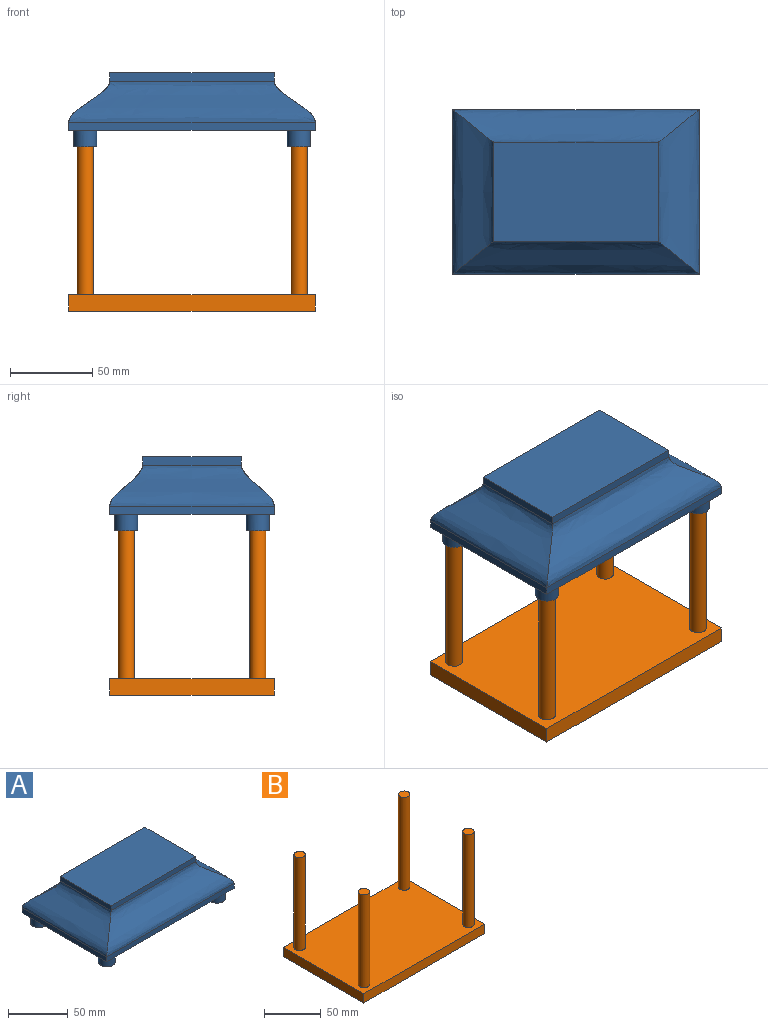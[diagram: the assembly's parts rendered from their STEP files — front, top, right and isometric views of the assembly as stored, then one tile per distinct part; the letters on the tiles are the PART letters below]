
ASSEMBLY  parts=2 mates=1
PART A: 43 faces, bbox 155x105x50 mm
  f0: plane 14x14mm, normal (0,0,-1), area 58.9mm2, adj f31,f38
  f1: plane 14x14mm, normal (0,0,-1), area 58.9mm2, adj f32,f37
  f2: plane 14x14mm, normal (0,0,-1), area 58.9mm2, adj f33,f36
  f3: plane 14x14mm, normal (0,0,-1), area 58.9mm2, adj f34,f35
  f4: plane 100x5mm, normal (-1,0,0), area 500mm2, adj f5,f7,f8,f17
  f5: plane 150x5mm, normal (0,-1,0), area 750mm2, adj f4,f6,f8,f14
  f6: plane 100x5mm, normal (1,0,0), area 500mm2, adj f5,f7,f8,f15
  f7: plane 150x5mm, normal (0,1,0), area 750mm2, adj f4,f6,f8,f16
  f8: plane 150x100mm, normal (0,0,-1), area 1225mm2, adj f4,f5,f6,f7,f18,f19,f20,f21
  f9: plane 100x5mm, normal (0,-1,0), area 500mm2, adj f10,f12,f13,f14
  f10: plane 60x5mm, normal (1,0,0), area 300mm2, adj f9,f11,f13,f15
  f11: plane 100x5mm, normal (0,1,0), area 500mm2, adj f10,f12,f13,f16
  f12: plane 60x5mm, normal (-1,0,0), area 300mm2, adj f9,f11,f13,f17
  f13: plane 100x60mm, normal (0,0,1), area 6000mm2, adj f9,f10,f11,f12
  f14: bspline ~150x25mm, area 4121.5mm2, adj f5,f9,f15,f17
  f15: bspline ~100x25mm, area 2923mm2, adj f6,f10,f14,f16
  f16: bspline ~150x25mm, area 4121.5mm2, adj f7,f11,f15,f17
  f17: bspline ~100x25mm, area 2923mm2, adj f4,f12,f14,f16
  f18: plane 95x5mm, normal (1,0,0), area 475mm2, adj f8,f19,f21,f30
  f19: plane 145x5mm, normal (0,1,0), area 725mm2, adj f8,f18,f20,f27
  f20: plane 95x5mm, normal (-1,0,0), area 475mm2, adj f8,f19,f21,f28
  f21: plane 145x5mm, normal (0,-1,0), area 725mm2, adj f8,f18,f20,f29
  f22: plane 95x2.5mm, normal (0,1,0), area 237.5mm2, adj f23,f25,f26,f27
  f23: plane 55x2.5mm, normal (-1,0,0), area 137.5mm2, adj f22,f24,f26,f28
  f24: plane 95x2.5mm, normal (0,-1,0), area 237.5mm2, adj f23,f25,f26,f29
  f25: plane 55x2.5mm, normal (1,0,0), area 137.5mm2, adj f22,f24,f26,f30
  f26: plane 95x55mm, normal (0,0,-1), area 5225mm2, adj f22,f23,f24,f25
  f27: offset ~155x30mm, area 3733.7mm2, adj f19,f22,f28,f30,f33,f34
  f28: offset ~105x30mm, area 2463.8mm2, adj f20,f23,f27,f29,f32,f33
  f29: offset ~155x30mm, area 3733.7mm2, adj f21,f24,f28,f30,f31,f32
  f30: offset ~105x30mm, area 2463.8mm2, adj f18,f25,f27,f29,f31,f34
  f31: cylinder r=7mm len=26.92mm, axis (0,0,-1), area 1018.7mm2, adj f0,f29,f30
  f32: cylinder r=7mm len=26.92mm, axis (0,0,-1), area 1018.7mm2, adj f1,f28,f29
  f33: cylinder r=7mm len=26.92mm, axis (0,0,-1), area 1018.7mm2, adj f2,f27,f28
  f34: cylinder r=7mm len=26.92mm, axis (0,0,-1), area 1018.7mm2, adj f3,f27,f30
  f35: cylinder r=5.5mm len=11mm, axis (0,0,-1), area 345.6mm2, adj f3,f39
  f36: cylinder r=5.5mm len=11mm, axis (0,0,-1), area 345.6mm2, adj f2,f40
  f37: cylinder r=5.5mm len=11mm, axis (0,0,-1), area 345.6mm2, adj f1,f41
  f38: cylinder r=5.5mm len=11mm, axis (0,0,-1), area 345.6mm2, adj f0,f42
  f39: plane 11x11mm, normal (0,0,-1), area 95mm2, adj f35
  f40: plane 11x11mm, normal (0,0,-1), area 95mm2, adj f36
  f41: plane 11x11mm, normal (0,0,-1), area 95mm2, adj f37
  f42: plane 11x11mm, normal (0,0,-1), area 95mm2, adj f38
PART B: 14 faces, bbox 150x100x110 mm
  f0: plane 150x10mm, normal (0,-1,0), area 1500mm2, adj f1,f3,f4,f5
  f1: plane 100x10mm, normal (1,0,0), area 1000mm2, adj f0,f2,f4,f5
  f2: plane 150x10mm, normal (0,1,0), area 1500mm2, adj f1,f3,f4,f5
  f3: plane 100x10mm, normal (-1,0,0), area 1000mm2, adj f0,f2,f4,f5
  f4: plane 150x100mm, normal (0,0,-1), area 15000mm2, adj f0,f1,f2,f3
  f5: plane 150x100mm, normal (0,0,1), area 14685.8mm2, adj f0,f1,f2,f3,f6,f8,f10,f12
  f6: cylinder r=5mm len=100mm, axis (0,0,-1), area 3141.6mm2, adj f5,f7
  f7: plane 10x10mm, normal (0,0,1), area 78.5mm2, adj f6
  f8: cylinder r=5mm len=100mm, axis (0,0,-1), area 3141.6mm2, adj f5,f9
  f9: plane 10x10mm, normal (0,0,1), area 78.5mm2, adj f8
  f10: cylinder r=5mm len=100mm, axis (0,0,-1), area 3141.6mm2, adj f5,f11
  f11: plane 10x10mm, normal (0,0,1), area 78.5mm2, adj f10
  f12: cylinder r=5mm len=100mm, axis (0,0,-1), area 3141.6mm2, adj f5,f13
  f13: plane 10x10mm, normal (0,0,1), area 78.5mm2, adj f12
PLACE A t=(-358.3,-61.16,-18.68)mm
PLACE B t=(-358.3,-61.16,-8.68)mm
MATE revolute B.f12 <-> A.f33  axis (0,0,1) through (-293.3,-101.16,91.32)mm
